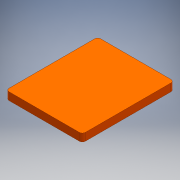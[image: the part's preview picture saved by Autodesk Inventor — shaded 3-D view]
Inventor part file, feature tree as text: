
AUTODESK INVENTOR PART (.ipt)
format: ipt  version: 2016 (Build 200138000, 138)  size: 123,392 bytes
history: native  units: mm
features: extrude x2, sketch x2
ambient origin geometry x8: Origin, YZ Plane, XZ Plane, XY Plane, X Axis, Y Axis, Z Axis, Center Point
bodies: Solid1 (feature_tree)
feature tree (4):
  extrude  "base"  Depth=50.0mm
  extrude  "magnetMount"  Depth=2.0mm
  sketch  "Sketch1"  dims[d0=60.0mm d1=50.0mm]
  sketch  "Sketch3"  dims[d2=30.0mm d3=25.0mm d4=2.0mm d5=5.0mm d6=0.0mm d7=2.65mm d8=2.65mm d9=2.65mm d10=2.65mm d11=2.65mm d12=15.0mm d13=15.0mm d14=15.0mm d15=15.0mm d16=2.0mm d17=0.0mm]
